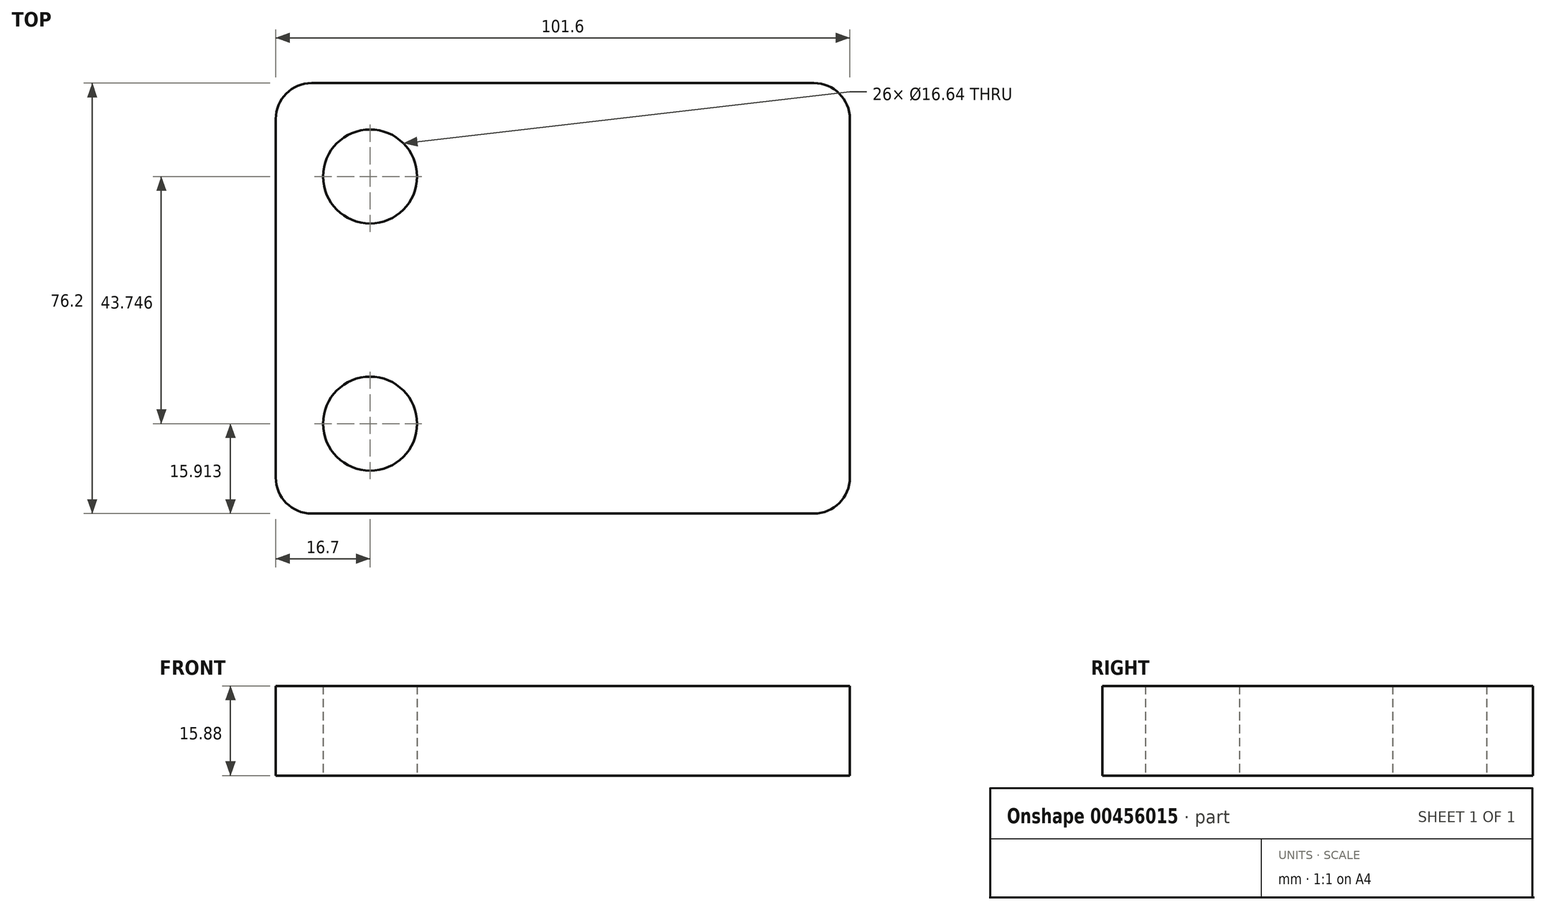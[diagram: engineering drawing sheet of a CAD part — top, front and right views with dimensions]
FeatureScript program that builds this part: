
annotation { "Feature Type Name" : "Feature", "Feature Type Description" : "" }
export const myFeature = defineFeature(function(context is Context, id is Id, definition is map)
    precondition{}
    {
        {
            var Q0;
            Q0=qCreatedBy(makeId("Top.planeOp"),FACE);
            var sketch = newSketch(context, id + "F0", { "sketchPlane" : qUnion([Q0])});
            skLineSegment(sketch, "E0.bottom", {"start": v(-45.75, 53.38) * mm, "end": v(43.15, 53.38) * mm});
            skLineSegment(sketch, "E0.top", {"start": v(-45.75, -22.82) * mm, "end": v(43.15, -22.82) * mm});
            skLineSegment(sketch, "E0.left", {"start": v(-52.1, 47.03) * mm, "end": v(-52.1, -16.47) * mm});
            skLineSegment(sketch, "E0.right", {"start": v(49.5, 47.03) * mm, "end": v(49.5, -16.47) * mm});
            skPoint(sketch, "E1.visualSharp", {"position": v(-52.1, 53.38) * mm});
            skArc(sketch, "E1.filletArc", {"start": v(-45.75, 53.38) * mm, "mid": v(-50.24, 51.52) * mm, "end": v(-52.1, 47.03) * mm});
            skPoint(sketch, "E2.visualSharp", {"position": v(-52.1, -22.82) * mm});
            skArc(sketch, "E2.filletArc", {"start": v(-52.1, -16.47) * mm, "mid": v(-50.24, -20.96) * mm, "end": v(-45.75, -22.82) * mm});
            skPoint(sketch, "E3.visualSharp", {"position": v(49.5, -22.82) * mm});
            skArc(sketch, "E3.filletArc", {"start": v(43.15, -22.82) * mm, "mid": v(47.65, -20.96) * mm, "end": v(49.5, -16.47) * mm});
            skPoint(sketch, "E4.visualSharp", {"position": v(49.5, 53.38) * mm});
            skArc(sketch, "E4.filletArc", {"start": v(49.5, 47.03) * mm, "mid": v(47.65, 51.52) * mm, "end": v(43.15, 53.38) * mm});
            skCircle(sketch, "E5", {"center": v(-35.4, 36.84) * mm, "radius": 8.32 * mm});
            skCircle(sketch, "E6", {"center": v(-35.4, -6.9) * mm, "radius": 8.32 * mm});
            skSolve(sketch);
        }
        {
            var Q0;
            Q0=makeQuery(id+"F0.imprint","IMPRINT",FACE,{"disambiguationData":[TD([[makeQuery(id+"F0.imprint","IMPRINT",EDGE,{"derivedFrom":sQuery(id+"F0.wireOp",EDGE,"E0.bottom")}),-1.0]])]});
            extrude(context, id + "F1", {"entities" : qUnion([Q0]), "depth" : 15.88 * mm});
        }
    });
